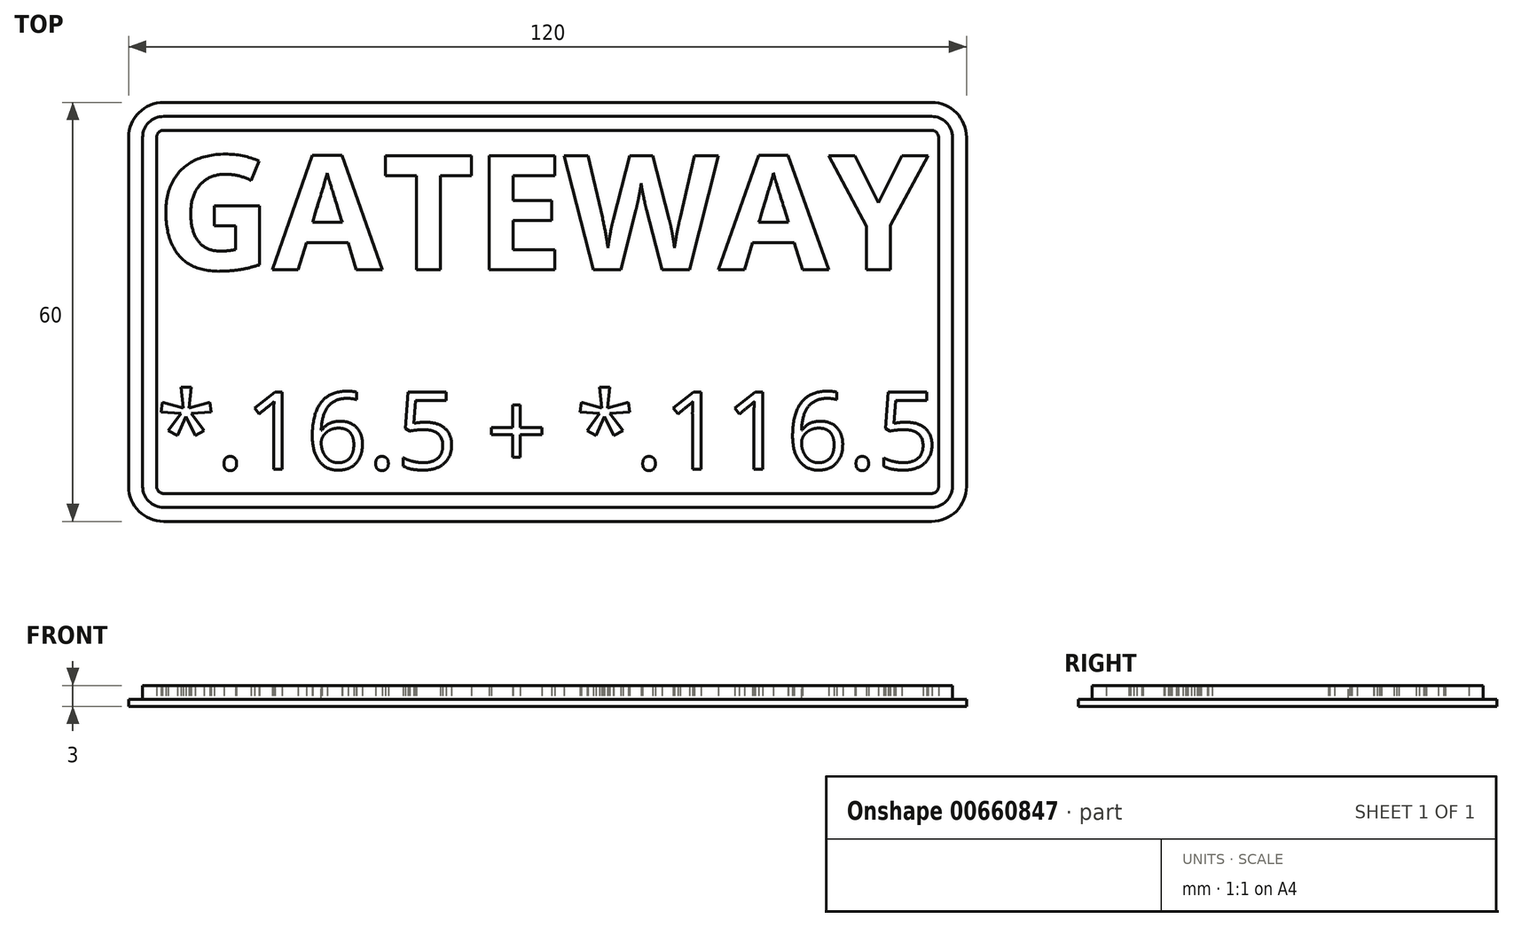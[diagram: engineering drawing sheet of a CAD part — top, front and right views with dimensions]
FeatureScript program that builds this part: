
annotation { "Feature Type Name" : "Feature", "Feature Type Description" : "" }
export const myFeature = defineFeature(function(context is Context, id is Id, definition is map)
    precondition{}
    {
        {
            assignVariable(context, id + "F0", {"variableType" : VariableType.LENGTH, "name" : "st", "lengthValue" : 1 * mm});
        }
        {
            assignVariable(context, id + "F1", {"variableType" : VariableType.LENGTH, "name" : "ft", "lengthValue" : 2 * mm});
        }
        {
            var Q0;
            Q0=qCreatedBy(makeId("Top.planeOp"),FACE);
            var sketch = newSketch(context, id + "F2", { "sketchPlane" : qUnion([Q0])});
            skLineSegment(sketch, "E0.bottom", {"start": v(-55, 30) * mm, "end": v(55, 30) * mm});
            skLineSegment(sketch, "E0.top", {"start": v(-55, -30) * mm, "end": v(55, -30) * mm});
            skLineSegment(sketch, "E0.left", {"start": v(-60, 25) * mm, "end": v(-60, -25) * mm});
            skLineSegment(sketch, "E0.right", {"start": v(60, 25) * mm, "end": v(60, -25) * mm});
            skPoint(sketch, "E1", {"position": v(0, 30) * mm});
            skPoint(sketch, "E2", {"position": v(-60, 0) * mm});
            skPoint(sketch, "E3.visualSharp", {"position": v(-60, 30) * mm});
            skArc(sketch, "E3.filletArc", {"start": v(-55, 30) * mm, "mid": v(-58.54, 28.54) * mm, "end": v(-60, 25) * mm});
            skPoint(sketch, "E4.visualSharp", {"position": v(60, 30) * mm});
            skArc(sketch, "E4.filletArc", {"start": v(60, 25) * mm, "mid": v(58.54, 28.54) * mm, "end": v(55, 30) * mm});
            skPoint(sketch, "E5.visualSharp", {"position": v(60, -30) * mm});
            skArc(sketch, "E5.filletArc", {"start": v(55, -30) * mm, "mid": v(58.54, -28.54) * mm, "end": v(60, -25) * mm});
            skPoint(sketch, "E6.visualSharp", {"position": v(-60, -30) * mm});
            skArc(sketch, "E6.filletArc", {"start": v(-60, -25) * mm, "mid": v(-58.54, -28.54) * mm, "end": v(-55, -30) * mm});
            skSolve(sketch);
        }
        {
            var Q0;
            Q0=qSketchRegion(id+"F2",true);
            extrude(context, id + "F3", {"entities" : qUnion([Q0]), "depth" : getVariable(context, 'st'), "offsetDistance" : 25 * mm});
        }
        {
            var Q0;
            Q0=makeQuery(id+"F3.opExtrude","CAP_FACE",FACE,{"disambiguationData":[OSD([sQuery(id+"F2.wireOp",EDGE,"E0.bottom"),sQuery(id+"F2.wireOp",EDGE,"E0.top"),sQuery(id+"F2.wireOp",EDGE,"E0.left"),sQuery(id+"F2.wireOp",EDGE,"E0.right"),sQuery(id+"F2.wireOp",EDGE,"E3.filletArc"),sQuery(id+"F2.wireOp",EDGE,"E4.filletArc"),sQuery(id+"F2.wireOp",EDGE,"E5.filletArc"),sQuery(id+"F2.wireOp",EDGE,"E6.filletArc")])],"isStart":false});
            var sketch = newSketch(context, id + "F4", { "sketchPlane" : qUnion([Q0])});
            skArc(sketch, "E7.0", {"start": v(-55, 28) * mm, "mid": v(-57.12, 27.12) * mm, "end": v(-58, 25) * mm});
            skLineSegment(sketch, "E7.1", {"start": v(-55, 28) * mm, "end": v(55, 28) * mm});
            skLineSegment(sketch, "E7.2", {"start": v(-58, 25) * mm, "end": v(-58, -25) * mm});
            skArc(sketch, "E7.3", {"start": v(58, 25) * mm, "mid": v(57.12, 27.12) * mm, "end": v(55, 28) * mm});
            skArc(sketch, "E7.4", {"start": v(-58, -25) * mm, "mid": v(-57.12, -27.12) * mm, "end": v(-55, -28) * mm});
            skLineSegment(sketch, "E7.5", {"start": v(-55, -28) * mm, "end": v(55, -28) * mm});
            skArc(sketch, "E7.6", {"start": v(55, -28) * mm, "mid": v(57.12, -27.12) * mm, "end": v(58, -25) * mm});
            skLineSegment(sketch, "E7.7", {"start": v(58, 25) * mm, "end": v(58, -25) * mm});
            skArc(sketch, "E8.0", {"start": v(-55, 26) * mm, "mid": v(-55.7, 25.7) * mm, "end": v(-56, 25) * mm});
            skLineSegment(sketch, "E8.1", {"start": v(-55, 26) * mm, "end": v(55, 26) * mm});
            skLineSegment(sketch, "E8.2", {"start": v(-56, 25) * mm, "end": v(-56, -25) * mm});
            skArc(sketch, "E8.3", {"start": v(56, 25) * mm, "mid": v(55.7, 25.7) * mm, "end": v(55, 26) * mm});
            skArc(sketch, "E8.4", {"start": v(-56, -25) * mm, "mid": v(-55.7, -25.7) * mm, "end": v(-55, -26) * mm});
            skLineSegment(sketch, "E8.5", {"start": v(-55, -26) * mm, "end": v(55, -26) * mm});
            skArc(sketch, "E8.6", {"start": v(55, -26) * mm, "mid": v(55.7, -25.7) * mm, "end": v(56, -25) * mm});
            skLineSegment(sketch, "E8.7", {"start": v(56, 25) * mm, "end": v(56, -25) * mm});
            skText(sketch, "E9", { "text": "GATEWAY", "fontName": "OpenSans-Bold.ttf"});
            skText(sketch, "E10", { "text": "*.16.5 + *.116.5", "fontName": "OpenSans-Regular.ttf"});
            skLineSegment(sketch, "E11", {"start": v(0, -22.51) * mm, "end": v(0, 22.51) * mm, "construction": true});
            const initialGuessF4  = {"E9": [-0.056, 0.00605, 1, 0, 0.01646], "E10": [-0.056, -0.02251, 1, 0, 0.0111]};
            skSetInitialGuess(sketch, initialGuessF4);
            skSolve(sketch);
        }
        {
            var Q0;
            Q0=makeQuery(id+"F4.imprint","IMPRINT",FACE,{"disambiguationData":[TD([[makeQuery(id+"F4.imprint","IMPRINT",EDGE,{"derivedFrom":sQuery(id+"F4.wireOp",EDGE,"E9.sketch_text.stroke-0")}),-1.0]])]});
            var Q1;
            Q1=makeQuery(id+"F4.imprint","IMPRINT",FACE,{"disambiguationData":[TD([[makeQuery(id+"F4.imprint","IMPRINT",EDGE,{"derivedFrom":sQuery(id+"F4.wireOp",EDGE,"E9.sketch_text.stroke-19")}),-1.0]])]});
            var Q2;
            Q2=makeQuery(id+"F4.imprint","IMPRINT",FACE,{"disambiguationData":[TD([[makeQuery(id+"F4.imprint","IMPRINT",EDGE,{"derivedFrom":sQuery(id+"F4.wireOp",EDGE,"E9.sketch_text.stroke-31")}),-1.0]])]});
            var Q3;
            Q3=makeQuery(id+"F4.imprint","IMPRINT",FACE,{"disambiguationData":[TD([[makeQuery(id+"F4.imprint","IMPRINT",EDGE,{"derivedFrom":sQuery(id+"F4.wireOp",EDGE,"E9.sketch_text.stroke-39")}),-1.0]])]});
            var Q4;
            Q4=makeQuery(id+"F4.imprint","IMPRINT",FACE,{"disambiguationData":[TD([[makeQuery(id+"F4.imprint","IMPRINT",EDGE,{"derivedFrom":sQuery(id+"F4.wireOp",EDGE,"E9.sketch_text.stroke-51")}),-1.0]])]});
            var Q5;
            Q5=makeQuery(id+"F4.imprint","IMPRINT",FACE,{"disambiguationData":[TD([[makeQuery(id+"F4.imprint","IMPRINT",EDGE,{"derivedFrom":sQuery(id+"F4.wireOp",EDGE,"E9.sketch_text.stroke-75")}),-1.0]])]});
            var Q6;
            Q6=makeQuery(id+"F4.imprint","IMPRINT",FACE,{"disambiguationData":[TD([[makeQuery(id+"F4.imprint","IMPRINT",EDGE,{"derivedFrom":sQuery(id+"F4.wireOp",EDGE,"E9.sketch_text.stroke-87")}),-1.0]])]});
            var Q7;
            Q7=makeQuery(id+"F4.imprint","IMPRINT",FACE,{"disambiguationData":[TD([[makeQuery(id+"F4.imprint","IMPRINT",EDGE,{"derivedFrom":sQuery(id+"F4.wireOp",EDGE,"E10.sketch_text.stroke-0")}),-1.0]])]});
            var Q8;
            Q8=makeQuery(id+"F4.imprint","IMPRINT",FACE,{"disambiguationData":[TD([[makeQuery(id+"F4.imprint","IMPRINT",EDGE,{"derivedFrom":sQuery(id+"F4.wireOp",EDGE,"E10.sketch_text.stroke-15")}),-1.0]])]});
            var Q9;
            Q9=makeQuery(id+"F4.imprint","IMPRINT",FACE,{"disambiguationData":[TD([[makeQuery(id+"F4.imprint","IMPRINT",EDGE,{"derivedFrom":sQuery(id+"F4.wireOp",EDGE,"E10.sketch_text.stroke-23")}),-1.0]])]});
            var Q10;
            Q10=makeQuery(id+"F4.imprint","IMPRINT",FACE,{"disambiguationData":[TD([[makeQuery(id+"F4.imprint","IMPRINT",EDGE,{"derivedFrom":sQuery(id+"F4.wireOp",EDGE,"E10.sketch_text.stroke-32")}),-1.0]])]});
            var Q11;
            Q11=makeQuery(id+"F4.imprint","IMPRINT",FACE,{"disambiguationData":[TD([[makeQuery(id+"F4.imprint","IMPRINT",EDGE,{"derivedFrom":sQuery(id+"F4.wireOp",EDGE,"E10.sketch_text.stroke-57")}),-1.0]])]});
            var Q12;
            Q12=makeQuery(id+"F4.imprint","IMPRINT",FACE,{"disambiguationData":[TD([[makeQuery(id+"F4.imprint","IMPRINT",EDGE,{"derivedFrom":sQuery(id+"F4.wireOp",EDGE,"E10.sketch_text.stroke-65")}),-1.0]])]});
            var Q13;
            Q13=makeQuery(id+"F4.imprint","IMPRINT",FACE,{"disambiguationData":[TD([[makeQuery(id+"F4.imprint","IMPRINT",EDGE,{"derivedFrom":sQuery(id+"F4.wireOp",EDGE,"E10.sketch_text.stroke-84")}),-1.0]])]});
            var Q14;
            Q14=makeQuery(id+"F4.imprint","IMPRINT",FACE,{"disambiguationData":[TD([[makeQuery(id+"F4.imprint","IMPRINT",EDGE,{"derivedFrom":sQuery(id+"F4.wireOp",EDGE,"E10.sketch_text.stroke-96")}),-1.0]])]});
            var Q15;
            Q15=makeQuery(id+"F4.imprint","IMPRINT",FACE,{"disambiguationData":[TD([[makeQuery(id+"F4.imprint","IMPRINT",EDGE,{"derivedFrom":sQuery(id+"F4.wireOp",EDGE,"E10.sketch_text.stroke-111")}),-1.0]])]});
            var Q16;
            Q16=makeQuery(id+"F4.imprint","IMPRINT",FACE,{"disambiguationData":[TD([[makeQuery(id+"F4.imprint","IMPRINT",EDGE,{"derivedFrom":sQuery(id+"F4.wireOp",EDGE,"E10.sketch_text.stroke-119")}),-1.0]])]});
            var Q17;
            Q17=makeQuery(id+"F4.imprint","IMPRINT",FACE,{"disambiguationData":[TD([[makeQuery(id+"F4.imprint","IMPRINT",EDGE,{"derivedFrom":sQuery(id+"F4.wireOp",EDGE,"E10.sketch_text.stroke-128")}),-1.0]])]});
            var Q18;
            Q18=makeQuery(id+"F4.imprint","IMPRINT",FACE,{"disambiguationData":[TD([[makeQuery(id+"F4.imprint","IMPRINT",EDGE,{"derivedFrom":sQuery(id+"F4.wireOp",EDGE,"E10.sketch_text.stroke-137")}),-1.0]])]});
            var Q19;
            Q19=makeQuery(id+"F4.imprint","IMPRINT",FACE,{"disambiguationData":[TD([[makeQuery(id+"F4.imprint","IMPRINT",EDGE,{"derivedFrom":sQuery(id+"F4.wireOp",EDGE,"E10.sketch_text.stroke-162")}),-1.0]])]});
            var Q20;
            Q20=makeQuery(id+"F4.imprint","IMPRINT",FACE,{"disambiguationData":[TD([[makeQuery(id+"F4.imprint","IMPRINT",EDGE,{"derivedFrom":sQuery(id+"F4.wireOp",EDGE,"E10.sketch_text.stroke-170")}),-1.0]])]});
            var Q21;
            Q21=makeQuery(id+"F4.imprint","IMPRINT",FACE,{"disambiguationData":[TD([[makeQuery(id+"F4.imprint","IMPRINT",EDGE,{"derivedFrom":sQuery(id+"F4.wireOp",EDGE,"E7.0")}),1.0]])]});
            extrude(context, id + "F5", {"entities" : qUnion([Q0, Q1, Q2, Q3, Q4, Q5, Q6, Q7, Q8, Q9, Q10, Q11, Q12, Q13, Q14, Q15, Q16, Q17, Q18, Q19, Q20, Q21]), "operationType" : NewBodyOperationType.ADD, "depth" : getVariable(context, 'ft'), "offsetDistance" : 25 * mm});
        }
    });
